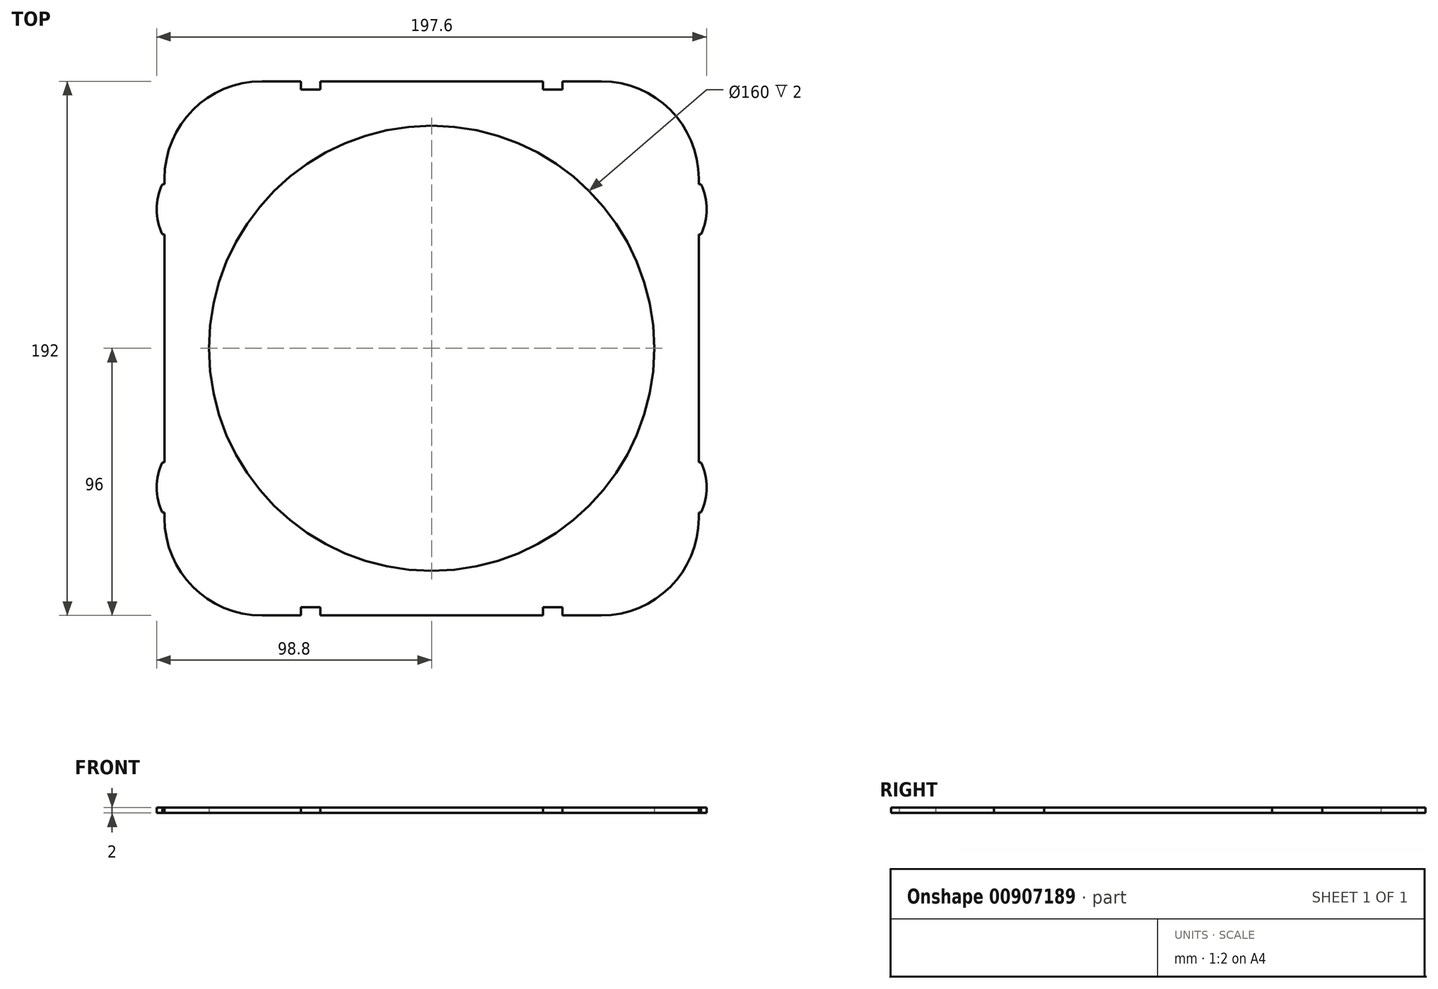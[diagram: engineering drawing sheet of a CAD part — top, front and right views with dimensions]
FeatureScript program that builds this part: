
annotation { "Feature Type Name" : "Feature", "Feature Type Description" : "" }
export const myFeature = defineFeature(function(context is Context, id is Id, definition is map)
    precondition{}
    {
        {
            var Q0;
            Q0=qCreatedBy(makeId("Top.planeOp"),FACE);
            var sketch = newSketch(context, id + "F0", { "sketchPlane" : qUnion([Q0])});
            skLineSegment(sketch, "E0.bottom", {"start": v(61, 96) * mm, "end": v(47, 96) * mm});
            skLineSegment(sketch, "E0.top", {"start": v(61, -96) * mm, "end": v(47, -96) * mm});
            skLineSegment(sketch, "E0.left", {"start": v(96, 61) * mm, "end": v(96, 41) * mm});
            skLineSegment(sketch, "E0.right", {"start": v(-96, 61) * mm, "end": v(-96, 41) * mm});
            skPoint(sketch, "E0.middle", {"position": v(0, 0) * mm});
            skCircle(sketch, "E1", {"center": v(0, 0) * mm, "radius": 80 * mm});
            skPoint(sketch, "E2.middle", {"position": v(-96, 0) * mm});
            skLineSegment(sketch, "E3.trimOffspring", {"start": v(-96, -41) * mm, "end": v(-96, -61) * mm});
            skLineSegment(sketch, "E4.trimOffspring", {"start": v(96, -41) * mm, "end": v(96, -61) * mm});
            skLineSegment(sketch, "E5.bottom", {"start": v(-96, 59) * mm, "end": v(-96.8, 59) * mm});
            skLineSegment(sketch, "E5.top", {"start": v(-96, 41) * mm, "end": v(-96.8, 41) * mm});
            skLineSegment(sketch, "E5.left", {"start": v(-96, 59) * mm, "end": v(-96, 41) * mm});
            skLineSegment(sketch, "E5.right", {"start": v(-96.8, 59) * mm, "end": v(-96.8, 41) * mm});
            skPoint(sketch, "E6", {"position": v(-96.8, 50) * mm});
            skLineSegment(sketch, "E7.MirrorCS", {"start": v(-96, -59) * mm, "end": v(-96.8, -59) * mm});
            skLineSegment(sketch, "E8.MirrorCS", {"start": v(-96.8, -59) * mm, "end": v(-96.8, -41) * mm});
            skLineSegment(sketch, "E9.MirrorCS", {"start": v(-96, -41) * mm, "end": v(-96.8, -41) * mm});
            skPoint(sketch, "E10", {"position": v(-96.8, -50) * mm});
            skPoint(sketch, "E11", {"position": v(-98.8, 50) * mm});
            skArc(sketch, "E12", {"start": v(-96.8, 59) * mm, "mid": v(-98.8, 50) * mm, "end": v(-96.8, 41) * mm});
            skArc(sketch, "E13.MirrorCS", {"start": v(-96.8, -59) * mm, "mid": v(-98.8, -50) * mm, "end": v(-96.8, -41) * mm});
            skLineSegment(sketch, "E14.MirrorCS", {"start": v(96, 59) * mm, "end": v(96.8, 59) * mm});
            skArc(sketch, "E15.MirrorCS", {"start": v(96.8, 59) * mm, "mid": v(98.8, 50) * mm, "end": v(96.8, 41) * mm});
            skLineSegment(sketch, "E16.MirrorCS", {"start": v(96, 41) * mm, "end": v(96.8, 41) * mm});
            skLineSegment(sketch, "E17.MirrorCS", {"start": v(96, -41) * mm, "end": v(96.8, -41) * mm});
            skArc(sketch, "E18.MirrorCS", {"start": v(96.8, -59) * mm, "mid": v(98.8, -50) * mm, "end": v(96.8, -41) * mm});
            skLineSegment(sketch, "E19.MirrorCS", {"start": v(96, -59) * mm, "end": v(96.8, -59) * mm});
            skLineSegment(sketch, "E20", {"start": v(-96, 41) * mm, "end": v(-96, -41) * mm});
            skLineSegment(sketch, "E21", {"start": v(96, 41) * mm, "end": v(96, -41) * mm});
            skLineSegment(sketch, "E22.top", {"start": v(-47, 93) * mm, "end": v(-40, 93) * mm});
            skLineSegment(sketch, "E22.left", {"start": v(-47, 96) * mm, "end": v(-47, 93) * mm});
            skLineSegment(sketch, "E22.right", {"start": v(-40, 96) * mm, "end": v(-40, 93) * mm});
            skLineSegment(sketch, "E23.trimOffspring", {"start": v(-47, 96) * mm, "end": v(-61, 96) * mm});
            skLineSegment(sketch, "E24.MirrorCS", {"start": v(47, 96) * mm, "end": v(47, 93) * mm});
            skLineSegment(sketch, "E25.MirrorCS", {"start": v(47, 93) * mm, "end": v(40, 93) * mm});
            skLineSegment(sketch, "E26.MirrorCS", {"start": v(40, 96) * mm, "end": v(40, 93) * mm});
            skLineSegment(sketch, "E27.MirrorCS", {"start": v(-47, -96) * mm, "end": v(-47, -93) * mm});
            skLineSegment(sketch, "E28.MirrorCS", {"start": v(-47, -93) * mm, "end": v(-40, -93) * mm});
            skLineSegment(sketch, "E29.MirrorCS", {"start": v(-40, -96) * mm, "end": v(-40, -93) * mm});
            skLineSegment(sketch, "E30.MirrorCS", {"start": v(40, -96) * mm, "end": v(40, -93) * mm});
            skLineSegment(sketch, "E31.MirrorCS", {"start": v(47, -93) * mm, "end": v(40, -93) * mm});
            skLineSegment(sketch, "E32.MirrorCS", {"start": v(47, -96) * mm, "end": v(47, -93) * mm});
            skLineSegment(sketch, "E33.trimOffspring", {"start": v(40, 96) * mm, "end": v(-40, 96) * mm});
            skLineSegment(sketch, "E34.trimOffspring", {"start": v(-47, -96) * mm, "end": v(-61, -96) * mm});
            skLineSegment(sketch, "E35.trimOffspring", {"start": v(40, -96) * mm, "end": v(-40, -96) * mm});
            skPoint(sketch, "E36.visualSharp", {"position": v(-96, -96) * mm});
            skArc(sketch, "E36.filletArc", {"start": v(-96, -61) * mm, "mid": v(-85.75, -85.75) * mm, "end": v(-61, -96) * mm});
            skPoint(sketch, "E37.visualSharp", {"position": v(96, -96) * mm});
            skArc(sketch, "E37.filletArc", {"start": v(61, -96) * mm, "mid": v(85.75, -85.75) * mm, "end": v(96, -61) * mm});
            skPoint(sketch, "E38.visualSharp", {"position": v(96, 96) * mm});
            skArc(sketch, "E38.filletArc", {"start": v(96, 61) * mm, "mid": v(85.75, 85.75) * mm, "end": v(61, 96) * mm});
            skPoint(sketch, "E39.visualSharp", {"position": v(-96, 96) * mm});
            skArc(sketch, "E39.filletArc", {"start": v(-61, 96) * mm, "mid": v(-85.75, 85.75) * mm, "end": v(-96, 61) * mm});
            skSolve(sketch);
        }
        {
            var Q0;
            {var subQ1=sQuery(id+"F0.wireOp",EDGE,"E17.MirrorCS");var subQ6=sQuery(id+"F0.wireOp",EDGE,"E5.bottom");var subQ12=makeQuery(id+"F0.imprint","IMPRINT",EDGE,{"derivedFrom":sQuery(id+"F0.wireOp",EDGE,"E5.right")});var subQ14=sQuery(id+"F0.wireOp",EDGE,"E14.MirrorCS");var subQ23=sQuery(id+"F0.wireOp",EDGE,"E7.MirrorCS");var subQ27=makeQuery(id+"F0.imprint","IMPRINT",EDGE,{"derivedFrom":sQuery(id+"F0.wireOp",EDGE,"E8.MirrorCS")});Q0=qUnion([makeQuery(id+"F0.imprint","IMPRINT",FACE,{"disambiguationData":[TD([[subQ12,-1.0]])]}),makeQuery(id+"F0.imprint","IMPRINT",FACE,{"disambiguationData":[TD([[makeQuery(id+"F0.imprint","IMPRINT",EDGE,{"derivedFrom":subQ23}),-1.0]])]}),makeQuery(id+"F0.imprint","IMPRINT",FACE,{"disambiguationData":[TD([[makeQuery(id+"F0.imprint","IMPRINT",EDGE,{"derivedFrom":subQ14}),-1.0]])]}),makeQuery(id+"F0.imprint","IMPRINT",FACE,{"disambiguationData":[TD([[subQ27,1.0]])]}),makeQuery(id+"F0.imprint","IMPRINT",FACE,{"disambiguationData":[TD([[makeQuery(id+"F0.imprint","IMPRINT",EDGE,{"derivedFrom":sQuery(id+"F0.wireOp",EDGE,"E0.bottom")}),1.0]])]}),makeQuery(id+"F0.imprint","IMPRINT",FACE,{"disambiguationData":[TD([[makeQuery(id+"F0.imprint","IMPRINT",EDGE,{"derivedFrom":subQ6}),1.0]])]}),makeQuery(id+"F0.imprint","IMPRINT",FACE,{"disambiguationData":[TD([[makeQuery(id+"F0.imprint","IMPRINT",EDGE,{"derivedFrom":subQ1}),-1.0]])]})]);}
            extrude(context, id + "F1", {"entities" : qUnion([Q0]), "depth" : 2 * mm});
        }
    });
